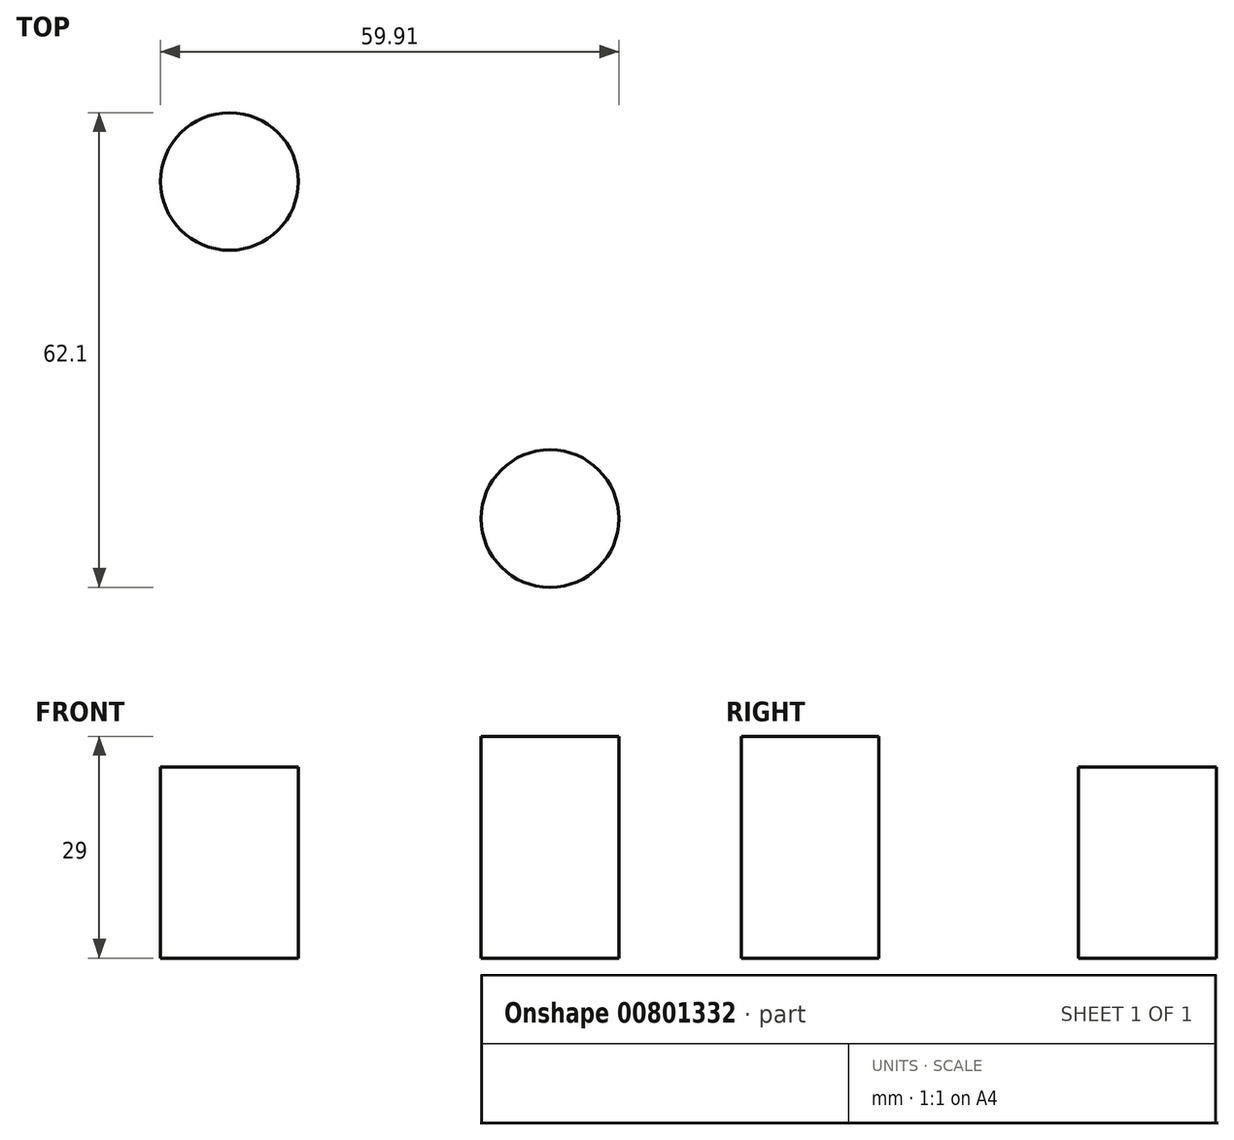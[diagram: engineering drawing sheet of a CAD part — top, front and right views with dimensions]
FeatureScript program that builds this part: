
annotation { "Feature Type Name" : "Feature", "Feature Type Description" : "" }
export const myFeature = defineFeature(function(context is Context, id is Id, definition is map)
    precondition{}
    {
        {
            var Q0;
            Q0=qCreatedBy(makeId("Top.planeOp"),FACE);
            var sketch = newSketch(context, id + "F0", { "sketchPlane" : qUnion([Q0])});
            skCircle(sketch, "E0", {"center": v(0, 0) * mm, "radius": 9 * mm});
            skSolve(sketch);
        }
        {
            var Q0;
            Q0=makeQuery(id+"F0.imprint","IMPRINT",FACE,{"disambiguationData":[TD([[makeQuery(id+"F0.imprint","IMPRINT",EDGE,{"derivedFrom":sQuery(id+"F0.wireOp",EDGE,"E0")}),1.0]])]});
            extrude(context, id + "F1", {"entities" : qUnion([Q0]), "depth" : 29 * mm, "offsetDistance" : 25 * mm});
        }
        {
            var Q0;
            Q0=qCreatedBy(makeId("Top.planeOp"),FACE);
            var sketch = newSketch(context, id + "F2", { "sketchPlane" : qUnion([Q0])});
            skCircle(sketch, "E1", {"center": v(-41.9, 44.1) * mm, "radius": 9 * mm});
            skSolve(sketch);
        }
        {
            var Q0;
            Q0 = qSketchRegion(id + "F2", true);
            extrude(context, id + "F3", {"entities" : qUnion([Q0]), "depth" : 25 * mm, "offsetDistance" : 25 * mm});
        }
    });
